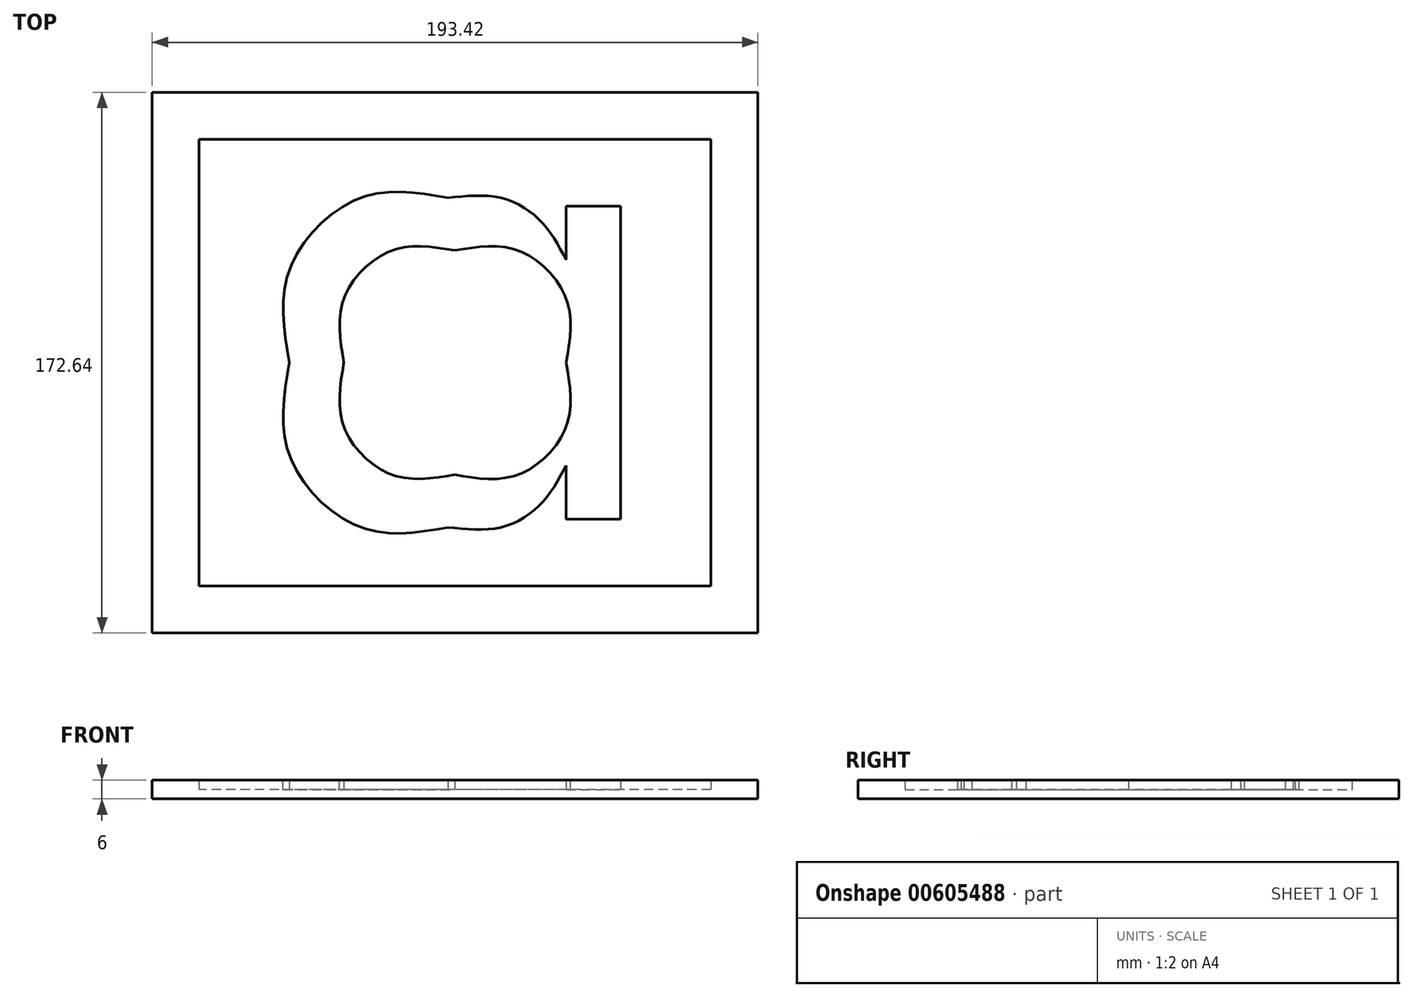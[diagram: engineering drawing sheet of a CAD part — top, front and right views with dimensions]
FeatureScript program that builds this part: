
annotation { "Feature Type Name" : "Feature", "Feature Type Description" : "" }
export const myFeature = defineFeature(function(context is Context, id is Id, definition is map)
    precondition{}
    {
        {
            var Q0;
            Q0=qCreatedBy(makeId("Top.planeOp"),FACE);
            var sketch = newSketch(context, id + "F0", { "sketchPlane" : qUnion([Q0])});
            skFitSpline(sketch, "E0", {"points": [v(35.5, 0) * mm, v(35.5, 20.4) * mm, v(20.1, 35.8) * mm, v(-0.1, 35.8) * mm]});
            skFitSpline(sketch, "E1", {"points": [v(-0.1, 35.8) * mm, v(-20.1, 35.8) * mm, v(-35.5, 20.4) * mm, v(-35.5, 0) * mm]});
            skFitSpline(sketch, "E2", {"points": [v(-35.5, 0) * mm, v(-35.5, -20.4) * mm, v(-20.1, -35.8) * mm, v(-0.1, -35.8) * mm]});
            skFitSpline(sketch, "E3", {"points": [v(-0.1, -35.8) * mm, v(20.1, -35.8) * mm, v(35.5, -20.4) * mm, v(35.5, 0) * mm]});
            skLineSegment(sketch, "E4", {"start": v(52.9, 50) * mm, "end": v(52.9, -50) * mm});
            skLineSegment(sketch, "E5", {"start": v(52.9, -50) * mm, "end": v(35.5, -50) * mm});
            skLineSegment(sketch, "E6", {"start": v(35.5, -50) * mm, "end": v(35.5, -32.8) * mm});
            skFitSpline(sketch, "E7", {"points": [v(35.5, -32.8) * mm, v(27.5, -45) * mm, v(14.7, -52.6) * mm, v(-2.3, -52.6) * mm]});
            skFitSpline(sketch, "E8", {"points": [v(-2.3, -52.6) * mm, v(-30.1, -52.6) * mm, v(-52.9, -29.6) * mm, v(-52.9, 0) * mm]});
            skFitSpline(sketch, "E9", {"points": [v(-52.9, 0) * mm, v(-52.9, 29.6) * mm, v(-30.1, 52.6) * mm, v(-2.3, 52.6) * mm]});
            skFitSpline(sketch, "E10", {"points": [v(-2.3, 52.6) * mm, v(14.7, 52.6) * mm, v(27.5, 45) * mm, v(35.5, 32.8) * mm]});
            skLineSegment(sketch, "E11", {"start": v(35.5, 32.8) * mm, "end": v(35.5, 50) * mm});
            skLineSegment(sketch, "E12", {"start": v(35.5, 50) * mm, "end": v(52.9, 50) * mm});
            skPoint(sketch, "E13.centerSnap0", {"position": v(44.2, -50) * mm});
            skLineSegment(sketch, "E14.bottom", {"start": v(-96.7, 86.32) * mm, "end": v(96.7, 86.32) * mm});
            skLineSegment(sketch, "E14.top", {"start": v(-96.7, -86.32) * mm, "end": v(96.7, -86.32) * mm});
            skLineSegment(sketch, "E14.left", {"start": v(-96.7, 86.32) * mm, "end": v(-96.7, -86.32) * mm});
            skLineSegment(sketch, "E14.right", {"start": v(96.7, 86.32) * mm, "end": v(96.7, -86.32) * mm});
            skLineSegment(sketch, "E15", {"start": v(0, 0) * mm, "end": v(0, 86.32) * mm, "construction": true});
            skLineSegment(sketch, "E16", {"start": v(0, 0) * mm, "end": v(96.7, 0) * mm, "construction": true});
            skLineSegment(sketch, "E17.0", {"start": v(-81.7, 71.32) * mm, "end": v(81.7, 71.32) * mm});
            skLineSegment(sketch, "E17.1", {"start": v(-81.7, 71.32) * mm, "end": v(-81.7, -71.32) * mm});
            skLineSegment(sketch, "E17.2", {"start": v(-81.7, -71.32) * mm, "end": v(81.7, -71.32) * mm});
            skLineSegment(sketch, "E17.3", {"start": v(81.7, 71.32) * mm, "end": v(81.7, -71.32) * mm});
            skSolve(sketch);
        }
        {
            var Q0;
            Q0=makeQuery(id+"F0.imprint","IMPRINT",FACE,{"disambiguationData":[TD([[makeQuery(id+"F0.imprint","IMPRINT",EDGE,{"derivedFrom":sQuery(id+"F0.wireOp",EDGE,"E14.bottom")}),-1.0]])]});
            var Q1;
            Q1=makeQuery(id+"F0.imprint","IMPRINT",FACE,{"disambiguationData":[TD([[makeQuery(id+"F0.imprint","IMPRINT",EDGE,{"derivedFrom":sQuery(id+"F0.wireOp",EDGE,"E4")}),1.0]])]});
            var Q2;
            Q2=makeQuery(id+"F0.imprint","IMPRINT",FACE,{"disambiguationData":[TD([[makeQuery(id+"F0.imprint","IMPRINT",EDGE,{"derivedFrom":sQuery(id+"F0.wireOp",EDGE,"E0")}),-1.0]])]});
            var Q3;
            Q3=makeQuery(id+"F0.imprint","IMPRINT",FACE,{"disambiguationData":[TD([[makeQuery(id+"F0.imprint","IMPRINT",EDGE,{"derivedFrom":sQuery(id+"F0.wireOp",EDGE,"E0")}),1.0]])]});
            extrude(context, id + "F1", {"entities" : qUnion([Q0, Q1, Q2, Q3]), "depth" : 3 * mm, "offsetDistance" : 25 * mm});
        }
        {
            var Q0;
            Q0=makeQuery(id+"F0.imprint","IMPRINT",FACE,{"disambiguationData":[TD([[makeQuery(id+"F0.imprint","IMPRINT",EDGE,{"derivedFrom":sQuery(id+"F0.wireOp",EDGE,"E14.bottom")}),-1.0]])]});
            var Q1;
            Q1=makeQuery(id+"F0.imprint","IMPRINT",FACE,{"disambiguationData":[TD([[makeQuery(id+"F0.imprint","IMPRINT",EDGE,{"derivedFrom":sQuery(id+"F0.wireOp",EDGE,"E0")}),-1.0]])]});
            extrude(context, id + "F2", {"entities" : qUnion([Q0, Q1]), "operationType" : NewBodyOperationType.ADD, "depth" : 6 * mm, "offsetDistance" : 25 * mm});
        }
    });
